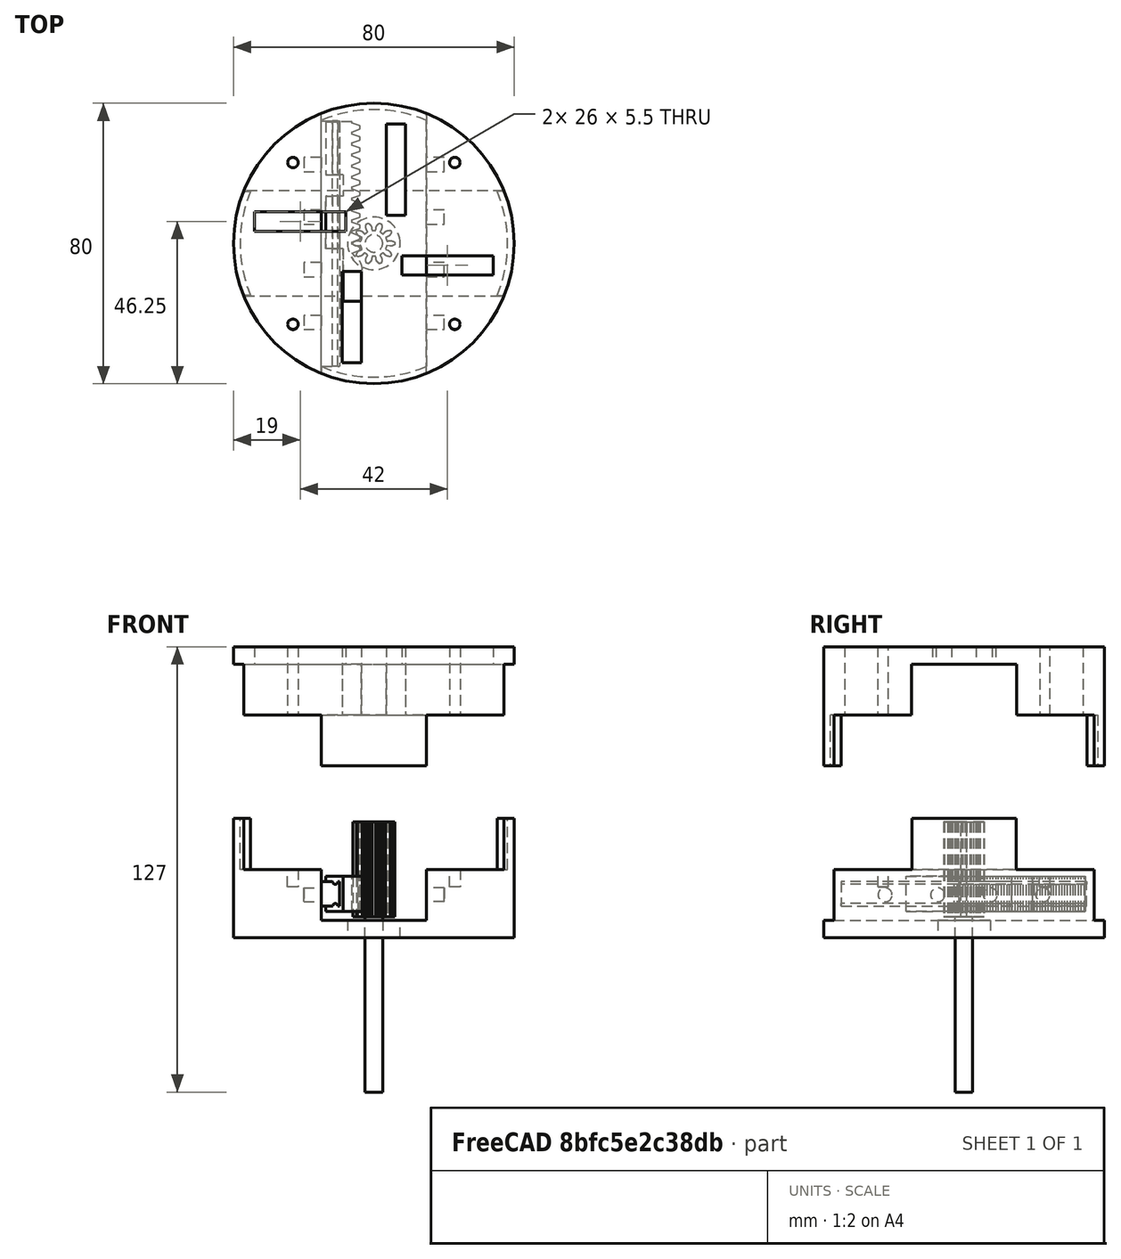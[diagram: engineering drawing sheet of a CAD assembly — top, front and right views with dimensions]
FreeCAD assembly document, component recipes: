
FREECAD ASSEMBLY — COMPONENT RECIPES ("2+2Jaw")

This assembly document has 7 components, labeled P0..P6 below (a component is one placed body or linked part). 7 of them carry a construction recipe — the FreeCAD feature program that regenerates the part from scratch, quoted from this document or its linked companion documents; the rest are supplied as boundary geometry only. No exploded tour is included for this assembly.
COMPONENT P0 — recipe-attached ("Jaw_Shell_Bottom001", modeled in this document).
Construction recipe (the document's own serialized feature program — sketch geometry with constraints, then the solid features built on it; lengths are millimeters unless a unit is written):

FEATURE [Sketcher::SketchObject] Sketch
  ArcFitTolerance = 1e-06
  AttachmentSupport = -> [Origin004]
  ExternalTypes = [0]
  FullyConstrained = true
  MakeInternals = false
  MapMode = 5
  _ExternalGeoVersion = 1
  sketch-geometry (2):
    g0: Circle CenterX=0 CenterY=0 CenterZ=0 NormalX=0 NormalY=0 NormalZ=1 AngleXU=0 Radius=40
    g1: Circle CenterX=0 CenterY=0 CenterZ=0 NormalX=0 NormalY=0 NormalZ=1 AngleXU=0 Radius=7.5
  constraints (4):
    c: Diameter(g0) = 80
    c: Coincident(g0,g-1)
    c: Diameter(g1) = 15
    c: Coincident(g1,g0)
FEATURE [PartDesign::Pad] Pad
  Direction = (0,0,1)
  Length = 34
  Length2 = 10
  Profile = -> Sketch
  ReferenceAxis = -> Sketch [N_Axis]
  Refine = true
  SideType = 0
  Suppressed = false
  Type = 0
  Type2 = 0
FEATURE [Part::DatumPlane] DatumPlane
  AttachmentSupport = -> [Origin004]
  MapMode = 5
  Placement = pos=(0,0,0) rot=(1,0,0;1.5708rad)
FEATURE [Sketcher::SketchObject] Sketch001
  ArcFitTolerance = 1e-06
  AttachmentSupport = -> [DatumPlane]
  ExternalGeometry = -> [Pad]
  ExternalTypes = [0,0,0]
  FullyConstrained = true
  MakeInternals = false
  MapMode = 5
  Placement = pos=(0,0,0) rot=(1,0,0;1.5708rad)
  _ExternalGeoVersion = 1
  sketch-geometry (5):
    g0: LineSegment StartX=-15 StartY=34 StartZ=0 EndX=-15 EndY=5 EndZ=0
    g1: LineSegment StartX=-15 StartY=5 StartZ=0 EndX=15 EndY=5 EndZ=0
    g2: LineSegment StartX=15 StartY=5 StartZ=0 EndX=15 EndY=34 EndZ=0
    g3: LineSegment StartX=-15 StartY=34 StartZ=0 EndX=0 EndY=34 EndZ=0
    g4: LineSegment StartX=0 StartY=34 StartZ=0 EndX=15 EndY=34 EndZ=0
  constraints (15):
    c: Coincident(g0,g1)
    c: Coincident(g1,g2)
    c: Vertical(g0)
    c: Vertical(g2)
    c: Horizontal(g1)
    c: Distance(g1,g-4) = 5
    c: Coincident(g0,g3)
    c: Horizontal(g3)
    c: Coincident(g3,g4)
    c: Horizontal(g4)
    c: PointOnObject(g3,g-2)
    c: Coincident(g4,g2)
    c: Equal(g3,g4)
    c: PointOnObject(g0,g-3)
    c: DistanceX(g1,g1) = 30
FEATURE [PartDesign::Pocket] Pocket
  BaseFeature = -> Pad
  Direction = (0,1,-2e-16)
  Length = 5
  Length2 = 5
  Profile = -> Sketch001
  ReferenceAxis = -> Sketch001 [N_Axis]
  Refine = true
  SideType = 2
  Suppressed = false
  Type = 1
  Type2 = 0
FEATURE [Sketcher::SketchObject] Sketch002
  ArcFitTolerance = 1e-06
  AttachmentSupport = -> [Pocket]
  ExternalGeometry = -> [Pocket]
  ExternalTypes = [0,0,0]
  FullyConstrained = true
  MakeInternals = false
  MapMode = 5
  Placement = pos=(0,0,34) rot=(0,0,1;0rad)
  _ExternalGeoVersion = 1
  sketch-geometry (16):
    g0: LineSegment StartX=35.1413 StartY=-14.85 StartZ=0 EndX=37.1413 EndY=-14.85 EndZ=0
    g1: LineSegment StartX=37.1413 StartY=14.85 StartZ=0 EndX=35.1413 EndY=14.85 EndZ=0
    g2: LineSegment [constr] StartX=37.1413 StartY=-14.85 StartZ=0 EndX=37.1413 EndY=0 EndZ=0
    g3: LineSegment [constr] StartX=37.1413 StartY=0 StartZ=0 EndX=37.1413 EndY=14.85 EndZ=0
    g4: ArcOfCircle CenterX=0 CenterY=0 CenterZ=0 NormalX=0 NormalY=0 NormalZ=1 AngleXU=0 Radius=38.1502 StartAngle=5.88337 EndAngle=6.683
    g5: LineSegment StartX=-35.1413 StartY=-14.85 StartZ=0 EndX=-37.1413 EndY=-14.85 EndZ=0
    g6: LineSegment StartX=-37.1413 StartY=14.85 StartZ=0 EndX=-35.1413 EndY=14.85 EndZ=0
    g7: LineSegment [constr] StartX=-37.1413 StartY=-14.85 StartZ=0 EndX=-37.1413 EndY=0 EndZ=0
    g8: LineSegment [constr] StartX=-37.1413 StartY=0 StartZ=0 EndX=-37.1413 EndY=14.85 EndZ=0
    g9: ArcOfCircle CenterX=0 CenterY=0 CenterZ=0 NormalX=0 NormalY=0 NormalZ=1 AngleXU=0 Radius=38.1502 StartAngle=2.74177 EndAngle=3.54141
    g10: LineSegment StartX=-37.1413 StartY=14.85 StartZ=0 EndX=-37.1413 EndY=40 EndZ=0
    g11: LineSegment StartX=-37.1413 StartY=40 StartZ=0 EndX=37.1413 EndY=40 EndZ=0
    g12: LineSegment StartX=-37.1413 StartY=-14.85 StartZ=0 EndX=-37.1413 EndY=-40 EndZ=0
    g13: LineSegment StartX=-37.1413 StartY=-40 StartZ=0 EndX=37.1413 EndY=-40 EndZ=0
    g14: LineSegment StartX=37.1413 StartY=-40 StartZ=0 EndX=37.1413 EndY=-14.85 EndZ=0
    g15: LineSegment StartX=37.1413 StartY=14.85 StartZ=0 EndX=37.1413 EndY=40 EndZ=0
  constraints (46):
    c: Horizontal(g0)
    c: Horizontal(g1)
    c: Coincident(g2,g0)
    c: PointOnObject(g2,g-1)
    c: Vertical(g2)
    c: Coincident(g3,g2)
    c: Coincident(g3,g1)
    c: Vertical(g3)
    c: Equal(g2,g3)
    c: PointOnObject(g1,g-3)
    c: Coincident(g4,g-3)
    c: Coincident(g4,g0)
    c: Coincident(g4,g1)
    c: Distance(g1,g1) = 2
    c: Horizontal(g5)
    c: Horizontal(g6)
    c: Coincident(g7,g5)
    c: Vertical(g7)
    c: Coincident(g8,g7)
    c: Coincident(g8,g6)
    c: Vertical(g8)
    c: Equal(g7,g8)
    c: Coincident(g9,g5)
    c: Coincident(g9,g6)
    c: Coincident(g9,g4)
    c: PointOnObject(g7,g-1)
    c: PointOnObject(g5,g-3)
    c: Equal(g7,g2)
    c: Distance(g5,g6) = 29.7
    c: Coincident(g6,g10)
    c: Vertical(g10)
    c: Coincident(g10,g11)
    c: Horizontal(g11)
    c: Coincident(g5,g12)
    c: Vertical(g12)
    c: Coincident(g12,g13)
    c: Horizontal(g13)
    c: Coincident(g13,g14)
    c: Coincident(g14,g0)
    c: Vertical(g14)
    c: Coincident(g15,g1)
    c: Coincident(g15,g11)
    c: Vertical(g15)
    c: Tangent(g13,g-3)
    c: Equal(g6,g1)
    c: Tangent(g11,g-3)
FEATURE [PartDesign::Pocket] Pocket001
  BaseFeature = -> Pocket
  Direction = (0,0,-1)
  Length = 14.5
  Length2 = 5
  Profile = -> Sketch002
  ReferenceAxis = -> Sketch002 [N_Axis]
  Refine = true
  SideType = 0
  Suppressed = false
  Type = 0
  Type2 = 0
FEATURE [Sketcher::SketchObject] Sketch003
  ArcFitTolerance = 1e-06
  AttachmentSupport = -> [Pocket001]
  ExternalGeometry = -> [Pocket001]
  ExternalTypes = [0,0,0,0]
  FullyConstrained = true
  MakeInternals = false
  MapMode = 5
  Placement = pos=(0,0,19.5) rot=(0,0,1;0rad)
  _ExternalGeoVersion = 1
  sketch-geometry (20):
    g0: Circle CenterX=-23.0923 CenterY=22.9991 CenterZ=0 NormalX=0 NormalY=0 NormalZ=1 AngleXU=0 Radius=1.5
    g1: ArcOfCircle [constr] CenterX=-45.3233 CenterY=45.1404 CenterZ=0 NormalX=0 NormalY=0 NormalZ=1 AngleXU=0 Radius=31.376 StartAngle=4.97621 EndAngle=6.02341
    g2: LineSegment [constr] StartX=-37.1413 StartY=14.85 StartZ=0 EndX=-23.0923 EndY=22.9991 EndZ=0
    g3: LineSegment [constr] StartX=-23.0923 StartY=22.9991 StartZ=0 EndX=-15 EndY=37.081 EndZ=0
    g4: LineSegment [constr] StartX=-37.1413 StartY=14.85 StartZ=0 EndX=-15 EndY=37.081 EndZ=0
    g5: ArcOfCircle [constr] CenterX=45.3233 CenterY=45.1404 CenterZ=0 NormalX=0 NormalY=0 NormalZ=1 AngleXU=0 Radius=31.376 StartAngle=3.40137 EndAngle=4.44857
    g6: ArcOfCircle [constr] CenterX=-45.3233 CenterY=-45.1404 CenterZ=0 NormalX=0 NormalY=0 NormalZ=1 AngleXU=0 Radius=31.376 StartAngle=0.259778 EndAngle=1.30698
    g7: ArcOfCircle [constr] CenterX=45.3233 CenterY=-45.1404 CenterZ=0 NormalX=0 NormalY=0 NormalZ=1 AngleXU=0 Radius=31.376 StartAngle=1.83462 EndAngle=2.88181
    g8: LineSegment [constr] StartX=-37.1413 StartY=-14.85 StartZ=0 EndX=-23.0923 EndY=-22.9991 EndZ=0
    g9: LineSegment [constr] StartX=-23.0923 StartY=-22.9991 StartZ=0 EndX=-15 EndY=-37.081 EndZ=0
    g10: LineSegment [constr] StartX=-15 StartY=-37.081 StartZ=0 EndX=-37.1413 EndY=-14.85 EndZ=0
    g11: LineSegment [constr] StartX=15 StartY=-37.081 StartZ=0 EndX=37.1413 EndY=-14.85 EndZ=0
    g12: LineSegment [constr] StartX=37.1413 StartY=-14.85 StartZ=0 EndX=23.0923 EndY=-22.9991 EndZ=0
    g13: LineSegment [constr] StartX=23.0923 StartY=-22.9991 StartZ=0 EndX=15 EndY=-37.081 EndZ=0
    g14: LineSegment [constr] StartX=15 StartY=37.081 StartZ=0 EndX=23.0923 EndY=22.9991 EndZ=0
    g15: LineSegment [constr] StartX=23.0923 StartY=22.9991 StartZ=0 EndX=37.1413 EndY=14.85 EndZ=0
    g16: LineSegment [constr] StartX=37.1413 StartY=14.85 StartZ=0 EndX=15 EndY=37.081 EndZ=0
    g17: Circle CenterX=23.0923 CenterY=22.9991 CenterZ=0 NormalX=0 NormalY=0 NormalZ=1 AngleXU=0 Radius=1.5
    g18: Circle CenterX=23.0923 CenterY=-22.9991 CenterZ=0 NormalX=0 NormalY=0 NormalZ=1 AngleXU=0 Radius=1.5
    g19: Circle CenterX=-23.0923 CenterY=-22.9991 CenterZ=0 NormalX=0 NormalY=0 NormalZ=1 AngleXU=0 Radius=1.5
  constraints (48):
    c: Diameter(g0) = 3
    c: Coincident(g1,g-6)
    c: Coincident(g1,g-6)
    c: PointOnObject(g0,g1)
    c: Coincident(g1,g2)
    c: Coincident(g2,g3)
    c: Coincident(g3,g1)
    c: Equal(g3,g2)
    c: Coincident(g2,g0)
    c: Coincident(g4,g1)
    c: Coincident(g4,g1)
    c: Angle(g2,g4) = 0.261799
    c: Coincident(g5,g-3)
    c: Coincident(g5,g-3)
    c: Coincident(g6,g-5)
    c: Coincident(g6,g-5)
    c: Coincident(g7,g-4)
    c: Coincident(g7,g-4)
    c: Coincident(g6,g8)
    c: Coincident(g8,g9)
    c: Coincident(g9,g6)
    c: Coincident(g9,g10)
    c: Coincident(g10,g8)
    c: Coincident(g7,g11)
    c: Coincident(g11,g12)
    c: Coincident(g12,g13)
    c: Coincident(g13,g11)
    c: Coincident(g5,g14)
    c: Coincident(g14,g15)
    c: Coincident(g15,g5)
    c: Coincident(g15,g16)
    c: Coincident(g16,g14)
    c: Equal(g8,g9)
    c: Equal(g15,g14)
    c: Equal(g12,g13)
    c: PointOnObject(g8,g6)
    c: PointOnObject(g12,g7)
    c: Coincident(g11,g7)
    c: PointOnObject(g14,g5)
    c: Angle(g10,g8) = 0.261799
    c: Angle(g12,g11) = 0.261799
    c: Angle(g16,g15) = 0.261799
    c: Coincident(g17,g14)
    c: Coincident(g18,g12)
    c: Coincident(g19,g8)
    c: Equal(g0,g17)
    c: Equal(g0,g19)
    c: Equal(g0,g18)
FEATURE [PartDesign::Pocket] Pocket002
  BaseFeature = -> Pocket001
  Direction = (0,0,-1)
  Length = 5
  Length2 = 5
  Profile = -> Sketch003
  ReferenceAxis = -> Sketch003 [N_Axis]
  Refine = true
  SideType = 0
  Suppressed = false
  Type = 0
  Type2 = 0
FEATURE [Sketcher::SketchObject] Sketch015
  ArcFitTolerance = 1e-06
  AttachmentSupport = -> [Pocket002]
  ExternalGeometry = -> [Pocket002]
  ExternalTypes = [0,0]
  FullyConstrained = true
  MakeInternals = false
  MapMode = 5
  Placement = pos=(-15,0,0) rot=(0.57735,0.57735,0.57735;2.0944rad)
  _ExternalGeoVersion = 1
  sketch-geometry (9):
    g0: Circle CenterX=22.5 CenterY=12.25 CenterZ=0 NormalX=0 NormalY=0 NormalZ=1 AngleXU=0 Radius=2
    g1: Circle CenterX=-22.5 CenterY=12.25 CenterZ=0 NormalX=0 NormalY=0 NormalZ=1 AngleXU=0 Radius=2
    g2: Circle CenterX=-7.5 CenterY=12.25 CenterZ=0 NormalX=0 NormalY=0 NormalZ=1 AngleXU=0 Radius=2
    g3: Circle CenterX=7.5 CenterY=12.25 CenterZ=0 NormalX=0 NormalY=0 NormalZ=1 AngleXU=0 Radius=2
    g4: LineSegment [constr] StartX=22.5 StartY=12.25 StartZ=0 EndX=7.5 EndY=12.25 EndZ=0
    g5: LineSegment [constr] StartX=7.5 StartY=12.25 StartZ=0 EndX=-7.5 EndY=12.25 EndZ=0
    g6: LineSegment [constr] StartX=-7.5 StartY=12.25 StartZ=0 EndX=-22.5 EndY=12.25 EndZ=0
    g7: LineSegment [constr] StartX=-22.5 StartY=12.25 StartZ=0 EndX=-37.081 EndY=12.25 EndZ=0
    g8: LineSegment [constr] StartX=22.5 StartY=12.25 StartZ=0 EndX=37.081 EndY=12.25 EndZ=0
  constraints (23):
    c: Diameter(g1) = 4
    c: Coincident(g0,g4)
    c: Coincident(g4,g3)
    c: Coincident(g4,g5)
    c: Coincident(g5,g2)
    c: Coincident(g5,g6)
    c: Coincident(g6,g1)
    c: Coincident(g6,g7)
    c: Horizontal(g7)
    c: Horizontal(g5)
    c: Horizontal(g6)
    c: Horizontal(g4)
    c: Equal(g1,g2)
    c: Equal(g1,g3)
    c: Equal(g1,g0)
    c: Equal(g6,g5)
    c: Equal(g6,g4)
    c: Equal(g8,g7)
    c: Horizontal(g8)
    c: PointOnObject(g7,g-4)
    c: Symmetric(g-3,g-3,g8)
    c: Coincident(g0,g8)
    c: DistanceX(g5,g5) = 15
FEATURE [Sketcher::SketchObject] Sketch016
  ArcFitTolerance = 1e-06
  AttachmentSupport = -> [Pocket002]
  ExternalGeometry = -> [Pocket002]
  ExternalTypes = [0,0]
  FullyConstrained = true
  MakeInternals = false
  MapMode = 5
  Placement = pos=(15,0,0) rot=(0.57735,-0.57735,-0.57735;2.0944rad)
  _ExternalGeoVersion = 1
  sketch-geometry (9):
    g0: Circle CenterX=22.5 CenterY=12.25 CenterZ=0 NormalX=0 NormalY=0 NormalZ=1 AngleXU=0 Radius=2
    g1: Circle CenterX=-22.5 CenterY=12.25 CenterZ=0 NormalX=0 NormalY=0 NormalZ=1 AngleXU=0 Radius=2
    g2: Circle CenterX=-7.5 CenterY=12.25 CenterZ=0 NormalX=0 NormalY=0 NormalZ=1 AngleXU=0 Radius=2
    g3: Circle CenterX=7.5 CenterY=12.25 CenterZ=0 NormalX=0 NormalY=0 NormalZ=1 AngleXU=0 Radius=2
    g4: LineSegment [constr] StartX=22.5 StartY=12.25 StartZ=0 EndX=7.5 EndY=12.25 EndZ=0
    g5: LineSegment [constr] StartX=7.5 StartY=12.25 StartZ=0 EndX=-7.5 EndY=12.25 EndZ=0
    g6: LineSegment [constr] StartX=-7.5 StartY=12.25 StartZ=0 EndX=-22.5 EndY=12.25 EndZ=0
    g7: LineSegment [constr] StartX=-22.5 StartY=12.25 StartZ=0 EndX=-37.081 EndY=12.25 EndZ=0
    g8: LineSegment [constr] StartX=22.5 StartY=12.25 StartZ=0 EndX=37.081 EndY=12.25 EndZ=0
  constraints (22):
    c: Diameter(g1) = 4
    c: Coincident(g0,g4)
    c: Coincident(g4,g3)
    c: Coincident(g4,g5)
    c: Coincident(g5,g2)
    c: Coincident(g5,g6)
    c: Coincident(g6,g1)
    c: Coincident(g6,g7)
    c: Horizontal(g7)
    c: Horizontal(g5)
    c: Horizontal(g6)
    c: Horizontal(g4)
    c: Equal(g1,g2)
    c: Equal(g1,g3)
    c: Equal(g1,g0)
    c: Equal(g6,g5)
    c: Equal(g6,g4)
    c: Equal(g8,g7)
    c: Symmetric(g-4,g-4,g8)
    c: Symmetric(g-3,g-3,g7)
    c: Coincident(g8,g0)
    c: DistanceX(g5,g5) = 15
FEATURE [PartDesign::Pocket] Pocket010
  BaseFeature = -> Pocket002
  Direction = (-1,0,0)
  Length = 5
  Length2 = 5
  Profile = -> Sketch015
  ReferenceAxis = -> Sketch015 [N_Axis]
  Refine = true
  SideType = 0
  Suppressed = false
  Type = 0
  Type2 = 0
FEATURE [PartDesign::Pocket] Pocket011
  BaseFeature = -> Pocket010
  Direction = (1,0,0)
  Length = 5
  Length2 = 5
  Profile = -> Sketch016
  ReferenceAxis = -> Sketch016 [N_Axis]
  Refine = true
  SideType = 0
  Suppressed = false
  Type = 0
  Type2 = 0
FEATURE [PartDesign::Body] Body  label="Jaw_Shell_Bottom"
  AllowCompound = true
  Group = -> [Sketch,Pad,DatumPlane,Sketch001,Pocket,Sketch002,Pocket001,Sketch003,Pocket002,Sketch015,Sketch016,Pocket010,Pocket011]
  Origin = -> Origin004
  Tip = -> Pocket011
COMPONENT P1 — recipe-attached ("Jaw_Shell_Top001", modeled in this document).
Construction recipe (the document's own serialized feature program — sketch geometry with constraints, then the solid features built on it; lengths are millimeters unless a unit is written):

FEATURE [Part::DatumPlane] DatumPlane001
  AttachmentSupport = -> [Origin006]
  MapMode = 5
  Placement = pos=(0,0,0) rot=(1,0,0;1.5708rad)
FEATURE [Sketcher::SketchObject] Sketch004
  ArcFitTolerance = 1e-06
  AttachmentSupport = -> [Origin006]
  ExternalTypes = [0]
  FullyConstrained = true
  MakeInternals = false
  MapMode = 5
  _ExternalGeoVersion = 1
  sketch-geometry (1):
    g0: Circle CenterX=0 CenterY=0 CenterZ=0 NormalX=0 NormalY=0 NormalZ=1 AngleXU=0 Radius=40
  constraints (2):
    c: Diameter(g0) = 80
    c: Coincident(g0,g-1)
FEATURE [PartDesign::Pad] Pad001
  Direction = (0,0,1)
  Length = 34
  Length2 = 10
  Profile = -> Sketch004
  ReferenceAxis = -> Sketch004 [N_Axis]
  Refine = true
  SideType = 0
  Suppressed = false
  Type = 0
  Type2 = 0
FEATURE [Sketcher::SketchObject] Sketch005
  ArcFitTolerance = 1e-06
  AttachmentSupport = -> [DatumPlane001]
  ExternalGeometry = -> [Pad001]
  ExternalTypes = [0,0,0]
  FullyConstrained = true
  MakeInternals = false
  MapMode = 5
  Placement = pos=(0,0,0) rot=(1,0,0;1.5708rad)
  _ExternalGeoVersion = 1
  sketch-geometry (5):
    g0: LineSegment StartX=-15 StartY=34 StartZ=0 EndX=-15 EndY=5 EndZ=0
    g1: LineSegment StartX=-15 StartY=5 StartZ=0 EndX=15 EndY=5 EndZ=0
    g2: LineSegment StartX=15 StartY=5 StartZ=0 EndX=15 EndY=34 EndZ=0
    g3: LineSegment StartX=-15 StartY=34 StartZ=0 EndX=0 EndY=34 EndZ=0
    g4: LineSegment StartX=0 StartY=34 StartZ=0 EndX=15 EndY=34 EndZ=0
  constraints (15):
    c: Coincident(g0,g1)
    c: Coincident(g1,g2)
    c: Vertical(g0)
    c: Vertical(g2)
    c: Horizontal(g1)
    c: Distance(g1,g-4) = 5
    c: Coincident(g0,g3)
    c: Horizontal(g3)
    c: Coincident(g3,g4)
    c: Horizontal(g4)
    c: PointOnObject(g3,g-2)
    c: Coincident(g4,g2)
    c: Equal(g3,g4)
    c: PointOnObject(g0,g-3)
    c: DistanceX(g1,g1) = 30
FEATURE [PartDesign::Pocket] Pocket003
  BaseFeature = -> Pad001
  Direction = (0,1,-2e-16)
  Length = 5
  Length2 = 5
  Profile = -> Sketch005
  ReferenceAxis = -> Sketch005 [N_Axis]
  Refine = true
  SideType = 2
  Suppressed = false
  Type = 1
  Type2 = 0
FEATURE [Sketcher::SketchObject] Sketch006
  ArcFitTolerance = 1e-06
  AttachmentSupport = -> [Pocket003]
  ExternalGeometry = -> [Pocket003]
  ExternalTypes = [0,0,0]
  FullyConstrained = true
  MakeInternals = false
  MapMode = 5
  Placement = pos=(0,0,34) rot=(0,0,1;0rad)
  _ExternalGeoVersion = 1
  sketch-geometry (16):
    g0: LineSegment StartX=35.081 StartY=-15 StartZ=0 EndX=37.081 EndY=-15 EndZ=0
    g1: LineSegment StartX=37.081 StartY=15 StartZ=0 EndX=35.081 EndY=15 EndZ=0
    g2: LineSegment [constr] StartX=37.081 StartY=-15 StartZ=0 EndX=37.081 EndY=0 EndZ=0
    g3: LineSegment [constr] StartX=37.081 StartY=0 StartZ=0 EndX=37.081 EndY=15 EndZ=0
    g4: ArcOfCircle CenterX=0 CenterY=0 CenterZ=0 NormalX=0 NormalY=0 NormalZ=1 AngleXU=0 Radius=38.1533 StartAngle=5.87913 EndAngle=6.68724
    g5: LineSegment StartX=-35.081 StartY=-15 StartZ=0 EndX=-37.081 EndY=-15 EndZ=0
    g6: LineSegment StartX=-37.081 StartY=15 StartZ=0 EndX=-35.081 EndY=15 EndZ=0
    g7: LineSegment [constr] StartX=-37.081 StartY=-15 StartZ=0 EndX=-37.081 EndY=0 EndZ=0
    g8: LineSegment [constr] StartX=-37.081 StartY=0 StartZ=0 EndX=-37.081 EndY=15 EndZ=0
    g9: ArcOfCircle CenterX=0 CenterY=0 CenterZ=0 NormalX=0 NormalY=0 NormalZ=1 AngleXU=0 Radius=38.1533 StartAngle=2.73754 EndAngle=3.54565
    g10: LineSegment StartX=-37.081 StartY=15 StartZ=0 EndX=-37.081 EndY=40 EndZ=0
    g11: LineSegment StartX=-37.081 StartY=40 StartZ=0 EndX=37.081 EndY=40 EndZ=0
    g12: LineSegment StartX=-37.081 StartY=-15 StartZ=0 EndX=-37.081 EndY=-40 EndZ=0
    g13: LineSegment StartX=-37.081 StartY=-40 StartZ=0 EndX=37.081 EndY=-40 EndZ=0
    g14: LineSegment StartX=37.081 StartY=-40 StartZ=0 EndX=37.081 EndY=-15 EndZ=0
    g15: LineSegment StartX=37.081 StartY=15 StartZ=0 EndX=37.081 EndY=40 EndZ=0
  constraints (46):
    c: Horizontal(g0)
    c: Horizontal(g1)
    c: Coincident(g2,g0)
    c: PointOnObject(g2,g-1)
    c: Vertical(g2)
    c: Coincident(g3,g2)
    c: Coincident(g3,g1)
    c: Vertical(g3)
    c: Equal(g2,g3)
    c: PointOnObject(g1,g-3)
    c: Coincident(g4,g-3)
    c: Coincident(g4,g0)
    c: Coincident(g4,g1)
    c: Distance(g1,g1) = 2
    c: Horizontal(g5)
    c: Horizontal(g6)
    c: Coincident(g7,g5)
    c: Vertical(g7)
    c: Coincident(g8,g7)
    c: Coincident(g8,g6)
    c: Vertical(g8)
    c: Equal(g7,g8)
    c: Coincident(g9,g5)
    c: Coincident(g9,g6)
    c: Coincident(g9,g4)
    c: PointOnObject(g7,g-1)
    c: PointOnObject(g5,g-3)
    c: Equal(g7,g2)
    c: Distance(g5,g6) = 30
    c: Coincident(g6,g10)
    c: Vertical(g10)
    c: Coincident(g10,g11)
    c: Horizontal(g11)
    c: Coincident(g5,g12)
    c: Vertical(g12)
    c: Coincident(g12,g13)
    c: Horizontal(g13)
    c: Coincident(g13,g14)
    c: Coincident(g14,g0)
    c: Vertical(g14)
    c: Coincident(g15,g1)
    c: Coincident(g15,g11)
    c: Vertical(g15)
    c: Tangent(g13,g-3)
    c: Equal(g6,g1)
    c: Tangent(g11,g-3)
FEATURE [PartDesign::Pocket] Pocket004
  BaseFeature = -> Pocket003
  Direction = (0,0,-1)
  Length = 14.5
  Length2 = 5
  Profile = -> Sketch006
  ReferenceAxis = -> Sketch006 [N_Axis]
  Refine = true
  SideType = 0
  Suppressed = false
  Type = 0
  Type2 = 0
FEATURE [Sketcher::SketchObject] Sketch007
  ArcFitTolerance = 1e-06
  AttachmentSupport = -> [Pocket004]
  ExternalGeometry = -> [Pocket004]
  ExternalTypes = [0,0,0,0]
  FullyConstrained = true
  MakeInternals = false
  MapMode = 5
  Placement = pos=(0,0,19.5) rot=(0,0,1;0rad)
  _ExternalGeoVersion = 1
  sketch-geometry (20):
    g0: Circle CenterX=-23.0822 CenterY=23.0822 CenterZ=0 NormalX=0 NormalY=0 NormalZ=1 AngleXU=0 Radius=1.5
    g1: ArcOfCircle [constr] CenterX=-45.1632 CenterY=45.1632 CenterZ=0 NormalX=0 NormalY=0 NormalZ=1 AngleXU=0 Radius=31.2272 StartAngle=4.97419 EndAngle=6.02139
    g2: LineSegment [constr] StartX=-37.081 StartY=15 StartZ=0 EndX=-23.0822 EndY=23.0822 EndZ=0
    g3: LineSegment [constr] StartX=-23.0822 StartY=23.0822 StartZ=0 EndX=-15 EndY=37.081 EndZ=0
    g4: LineSegment [constr] StartX=-37.081 StartY=15 StartZ=0 EndX=-15 EndY=37.081 EndZ=0
    g5: ArcOfCircle [constr] CenterX=45.1632 CenterY=45.1632 CenterZ=0 NormalX=0 NormalY=0 NormalZ=1 AngleXU=0 Radius=31.2272 StartAngle=3.40339 EndAngle=4.45059
    g6: ArcOfCircle [constr] CenterX=-45.1632 CenterY=-45.1632 CenterZ=0 NormalX=0 NormalY=0 NormalZ=1 AngleXU=0 Radius=31.2272 StartAngle=0.261799 EndAngle=1.309
    g7: ArcOfCircle [constr] CenterX=45.1632 CenterY=-45.1632 CenterZ=0 NormalX=0 NormalY=0 NormalZ=1 AngleXU=0 Radius=31.2272 StartAngle=1.8326 EndAngle=2.87979
    g8: LineSegment [constr] StartX=-37.081 StartY=-15 StartZ=0 EndX=-23.0822 EndY=-23.0822 EndZ=0
    g9: LineSegment [constr] StartX=-23.0822 StartY=-23.0822 StartZ=0 EndX=-15 EndY=-37.081 EndZ=0
    g10: LineSegment [constr] StartX=-15 StartY=-37.081 StartZ=0 EndX=-37.081 EndY=-15 EndZ=0
    g11: LineSegment [constr] StartX=15 StartY=-37.081 StartZ=0 EndX=37.081 EndY=-15 EndZ=0
    g12: LineSegment [constr] StartX=37.081 StartY=-15 StartZ=0 EndX=23.0822 EndY=-23.0822 EndZ=0
    g13: LineSegment [constr] StartX=23.0822 StartY=-23.0822 StartZ=0 EndX=15 EndY=-37.081 EndZ=0
    g14: LineSegment [constr] StartX=15 StartY=37.081 StartZ=0 EndX=23.0822 EndY=23.0822 EndZ=0
    g15: LineSegment [constr] StartX=23.0822 StartY=23.0822 StartZ=0 EndX=37.081 EndY=15 EndZ=0
    g16: LineSegment [constr] StartX=37.081 StartY=15 StartZ=0 EndX=15 EndY=37.081 EndZ=0
    g17: Circle CenterX=23.0822 CenterY=23.0822 CenterZ=0 NormalX=0 NormalY=0 NormalZ=1 AngleXU=0 Radius=1.5
    g18: Circle CenterX=23.0822 CenterY=-23.0822 CenterZ=0 NormalX=0 NormalY=0 NormalZ=1 AngleXU=0 Radius=1.5
    g19: Circle CenterX=-23.0822 CenterY=-23.0822 CenterZ=0 NormalX=0 NormalY=0 NormalZ=1 AngleXU=0 Radius=1.5
  constraints (48):
    c: Diameter(g0) = 3
    c: Coincident(g1,g-6)
    c: Coincident(g1,g-6)
    c: PointOnObject(g0,g1)
    c: Coincident(g1,g2)
    c: Coincident(g2,g3)
    c: Coincident(g3,g1)
    c: Equal(g3,g2)
    c: Coincident(g2,g0)
    c: Coincident(g4,g1)
    c: Coincident(g4,g1)
    c: Angle(g2,g4) = 0.261799
    c: Coincident(g5,g-3)
    c: Coincident(g5,g-3)
    c: Coincident(g6,g-5)
    c: Coincident(g6,g-5)
    c: Coincident(g7,g-4)
    c: Coincident(g7,g-4)
    c: Coincident(g6,g8)
    c: Coincident(g8,g9)
    c: Coincident(g9,g6)
    c: Coincident(g9,g10)
    c: Coincident(g10,g8)
    c: Coincident(g7,g11)
    c: Coincident(g11,g12)
    c: Coincident(g12,g13)
    c: Coincident(g13,g11)
    c: Coincident(g5,g14)
    c: Coincident(g14,g15)
    c: Coincident(g15,g5)
    c: Coincident(g15,g16)
    c: Coincident(g16,g14)
    c: Equal(g8,g9)
    c: Equal(g15,g14)
    c: Equal(g12,g13)
    c: PointOnObject(g8,g6)
    c: PointOnObject(g12,g7)
    c: Coincident(g11,g7)
    c: PointOnObject(g14,g5)
    c: Angle(g10,g8) = 0.261799
    c: Angle(g12,g11) = 0.261799
    c: Angle(g16,g15) = 0.261799
    c: Coincident(g17,g14)
    c: Coincident(g18,g12)
    c: Coincident(g19,g8)
    c: Equal(g0,g17)
    c: Equal(g0,g19)
    c: Equal(g0,g18)
FEATURE [PartDesign::Pocket] Pocket005
  BaseFeature = -> Pocket004
  Direction = (0,0,-1)
  Length = 5
  Length2 = 5
  Profile = -> Sketch007
  ReferenceAxis = -> Sketch007 [N_Axis]
  Refine = true
  SideType = 0
  Suppressed = false
  Type = 1
  Type2 = 0
FEATURE [Sketcher::SketchObject] Sketch014
  ArcFitTolerance = 1e-06
  AttachmentSupport = -> [Pocket004]
  ExternalTypes = [0]
  FullyConstrained = true
  MakeInternals = false
  MapMode = 5
  Placement = pos=(0,0,0) rot=(1,0,0;3.14159rad)
  _ExternalGeoVersion = 1
  sketch-geometry (24):
    g0: LineSegment StartX=3.5 StartY=34 StartZ=0 EndX=3.5 EndY=8 EndZ=0
    g1: LineSegment StartX=3.5 StartY=8 StartZ=0 EndX=9 EndY=8 EndZ=0
    g2: LineSegment StartX=9 StartY=8 StartZ=0 EndX=9 EndY=34 EndZ=0
    g3: LineSegment StartX=9 StartY=34 StartZ=0 EndX=3.5 EndY=34 EndZ=0
    g4: LineSegment StartX=8 StartY=-3.5 StartZ=0 EndX=8 EndY=-9 EndZ=0
    g5: LineSegment StartX=8 StartY=-9 StartZ=0 EndX=34 EndY=-9 EndZ=0
    g6: LineSegment StartX=34 StartY=-9 StartZ=0 EndX=34 EndY=-3.5 EndZ=0
    g7: LineSegment StartX=34 StartY=-3.5 StartZ=0 EndX=8 EndY=-3.5 EndZ=0
    g8: LineSegment StartX=-9 StartY=-8 StartZ=0 EndX=-9 EndY=-34 EndZ=0
    g9: LineSegment StartX=-9 StartY=-34 StartZ=0 EndX=-3.5 EndY=-34 EndZ=0
    g10: LineSegment StartX=-3.5 StartY=-34 StartZ=0 EndX=-3.5 EndY=-8 EndZ=0
    g11: LineSegment StartX=-3.5 StartY=-8 StartZ=0 EndX=-9 EndY=-8 EndZ=0
    g12: LineSegment StartX=-8 StartY=9 StartZ=0 EndX=-34 EndY=9 EndZ=0
    g13: LineSegment StartX=-34 StartY=9 StartZ=0 EndX=-34 EndY=3.5 EndZ=0
    g14: LineSegment StartX=-34 StartY=3.5 StartZ=0 EndX=-8 EndY=3.5 EndZ=0
    g15: LineSegment StartX=-8 StartY=3.5 StartZ=0 EndX=-8 EndY=9 EndZ=0
    g16: LineSegment [constr] StartX=3.5 StartY=0 StartZ=0 EndX=3.5 EndY=8 EndZ=0
    g17: LineSegment [constr] StartX=0 StartY=8 StartZ=0 EndX=3.5 EndY=8 EndZ=0
    g18: LineSegment [constr] StartX=-8 StartY=0 StartZ=0 EndX=-8 EndY=3.5 EndZ=0
    g19: LineSegment [constr] StartX=-8 StartY=3.5 StartZ=0 EndX=0 EndY=3.5 EndZ=0
    g20: LineSegment [constr] StartX=0 StartY=-8 StartZ=0 EndX=-3.5 EndY=-8 EndZ=0
    g21: LineSegment [constr] StartX=-3.5 StartY=-8 StartZ=0 EndX=-3.5 EndY=0 EndZ=0
    g22: LineSegment [constr] StartX=0 StartY=-3.5 StartZ=0 EndX=8 EndY=-3.5 EndZ=0
    g23: LineSegment [constr] StartX=8 StartY=0 StartZ=0 EndX=8 EndY=-3.5 EndZ=0
  constraints (72):
    c: Coincident(g0,g1)
    c: Coincident(g1,g2)
    c: Coincident(g2,g3)
    c: Coincident(g3,g0)
    c: Vertical(g0)
    c: Vertical(g2)
    c: Horizontal(g1)
    c: Horizontal(g3)
    c: Coincident(g4,g5)
    c: Coincident(g5,g6)
    c: Coincident(g6,g7)
    c: Coincident(g7,g4)
    c: Vertical(g4)
    c: Vertical(g6)
    c: Horizontal(g5)
    c: Horizontal(g7)
    c: Distance(g4,g6) = 26
    c: Distance(g5,g7) = 5.5
    c: Coincident(g8,g9)
    c: Coincident(g9,g10)
    c: Coincident(g10,g11)
    c: Coincident(g11,g8)
    c: Vertical(g8)
    c: Vertical(g10)
    c: Horizontal(g9)
    c: Horizontal(g11)
    c: Coincident(g12,g13)
    c: Coincident(g13,g14)
    c: Coincident(g14,g15)
    c: Coincident(g15,g12)
    c: Horizontal(g12)
    c: Horizontal(g14)
    c: Vertical(g13)
    c: Vertical(g15)
    c: Distance(g-1,g7) = 3.5
    c: Equal(g5,g2)
    c: Equal(g5,g14)
    c: Equal(g5,g8)
    c: PointOnObject(g16,g-1)
    c: Coincident(g16,g0)
    c: PointOnObject(g17,g-2)
    c: Coincident(g17,g0)
    c: PointOnObject(g18,g-1)
    c: Coincident(g18,g14)
    c: Coincident(g19,g14)
    c: PointOnObject(g19,g-2)
    c: Horizontal(g19)
    c: PointOnObject(g20,g-2)
    c: Coincident(g20,g10)
    c: Coincident(g21,g10)
    c: PointOnObject(g21,g-1)
    c: PointOnObject(g22,g-2)
    c: Coincident(g22,g4)
    c: PointOnObject(g23,g-1)
    c: Coincident(g23,g4)
    c: Horizontal(g17)
    c: Horizontal(g22)
    c: Horizontal(g20)
    c: Vertical(g21)
    c: Vertical(g18)
    c: Vertical(g23)
    c: Vertical(g16)
    c: Distance(g-2,g4) = 8
    c: Equal(g22,g16)
    c: Equal(g22,g19)
    c: Equal(g22,g21)
    c: Equal(g23,g17)
    c: Equal(g23,g18)
    c: Equal(g23,g20)
    c: Equal(g4,g1)
    c: Equal(g4,g11)
    c: Equal(g4,g15)
FEATURE [PartDesign::Pocket] Pocket009
  BaseFeature = -> Pocket005
  Direction = (0,0,1)
  Length = 5
  Length2 = 5
  Profile = -> Sketch014
  ReferenceAxis = -> Sketch014 [N_Axis]
  Refine = true
  SideType = 0
  Suppressed = false
  Type = 1
  Type2 = 0
FEATURE [PartDesign::Body] Body001  label="Jaw_Shell_Top"
  AllowCompound = true
  Group = -> [Sketch004,Pad001,DatumPlane001,Sketch005,Pocket003,Sketch006,Pocket004,Sketch007,Pocket005,Sketch014,Pocket009]
  Origin = -> Origin006
  Placement = pos=(-3.8e-15,3.8e-15,83) rot=(0.707107,0.707107,0;3.14159rad)
  Tip = -> Pocket009
COMPONENT P2 — recipe-attached ("Rack001", modeled in this document).
Construction recipe (the document's own serialized feature program — sketch geometry with constraints, then the solid features built on it; lengths are millimeters unless a unit is written):

FEATURE [PartDesign::FeaturePython] InvoluteRack  # WARN: FeaturePython — macro-defined, semantics opaque (R4)
  AttacherType = Attacher::AttachEngine3D
  Suppressed = false
  add_endings = true
  clearance = 0.25
  double_helix = false
  head = 0
  head_fillet = 0
  height = 10
  helix_angle = 0
  module = 1
  num_teeth = 12
  pressure_angle = 20
  properties_from_tool = false
  root_fillet = 0
  simplified = false
  thickness = 1
  transverse_pitch = 3.14159
  version = 1.3.0
FEATURE [Sketcher::SketchObject] Sketch009
  ArcFitTolerance = 1e-06
  AttachmentSupport = -> [InvoluteRack]
  ExternalGeometry = -> [InvoluteRack]
  ExternalTypes = [0,0,0]
  FullyConstrained = true
  MakeInternals = false
  MapMode = 5
  Placement = pos=(0,0,0) rot=(1,0,0;3.14159rad)
  _ExternalGeoVersion = 1
  sketch-geometry (10):
    g0: ArcOfCircle CenterX=2.74624 CenterY=-1.76464 CenterZ=0 NormalX=0 NormalY=0 NormalZ=1 AngleXU=0 Radius=5 StartAngle=2.2143 EndAngle=3.10281
    g1: LineSegment StartX=-3.75 StartY=-36.1283 StartZ=0 EndX=-3.75 EndY=15 EndZ=0
    g2: LineSegment StartX=-3.75 StartY=15 StartZ=0 EndX=1.74624 EndY=15 EndZ=0
    g3: LineSegment StartX=1.74624 StartY=15 StartZ=0 EndX=1.74624 EndY=6.23536 EndZ=0
    g4: ArcOfCircle CenterX=-3.25376 CenterY=6.23536 CenterZ=0 NormalX=0 NormalY=0 NormalZ=1 AngleXU=0 Radius=5 StartAngle=5.35589 EndAngle=6.28319
    g5: LineSegment [constr] StartX=2.74624 StartY=-1.76464 StartZ=0 EndX=2.74624 EndY=15 EndZ=0
    g6: LineSegment [constr] StartX=1.74624 StartY=15 StartZ=0 EndX=2.74624 EndY=15 EndZ=0
    g7: LineSegment [constr] StartX=-2.25 StartY=-1.5708 StartZ=0 EndX=-1.25 EndY=-1.5708 EndZ=0
    g8: LineSegment StartX=-2.25 StartY=-1.5708 StartZ=0 EndX=-2.25 EndY=-36.1283 EndZ=0
    g9: LineSegment StartX=-2.25 StartY=-36.1283 StartZ=0 EndX=-3.75 EndY=-36.1283 EndZ=0
  constraints (27):
    c: Radius(g0) = 5
    c: Vertical(g1)
    c: Coincident(g1,g2)
    c: Horizontal(g2)
    c: Coincident(g2,g3)
    c: Vertical(g3)
    c: Coincident(g5,g0)
    c: Vertical(g5)
    c: Coincident(g6,g2)
    c: Coincident(g6,g5)
    c: Horizontal(g6)
    c: Tangent(g4,g0) = 1.5708
    c: Tangent(g4,g3) = 1.5708
    c: PointOnObject(g-3,g0)
    c: Distance(g-1,g2) = 15
    c: Equal(g4,g0)
    c: Coincident(g7,g0)
    c: Symmetric(g-4,g-4,g7)
    c: Horizontal(g7)
    c: Distance(g3,g5) = 1
    c: Coincident(g8,g0)
    c: Coincident(g8,g-5)
    c: Vertical(g8)
    c: Coincident(g9,g8)
    c: Coincident(g9,g1)
    c: Horizontal(g9)
    c: Distance(g9,g9) = 1.5
FEATURE [PartDesign::Pad] Pad006
  BaseFeature = -> InvoluteRack
  Direction = (0,0,-1)
  Length = 10
  Length2 = 10
  Profile = -> Sketch009
  ReferenceAxis = -> Sketch009 [N_Axis]
  Refine = true
  SideType = 0
  Suppressed = false
  Type = 3
  Type2 = 0
  UpToFace = -> InvoluteRack [Face54]
FEATURE [Sketcher::SketchObject] Sketch010
  ArcFitTolerance = 1e-06
  AttachmentSupport = -> [Pad006]
  ExternalGeometry = -> [Pad006]
  ExternalTypes = [0]
  FullyConstrained = true
  MakeInternals = false
  MapMode = 5
  Placement = pos=(-3.75,0,0) rot=(0.57735,-0.57735,-0.57735;2.0944rad)
  _ExternalGeoVersion = 1
  sketch-geometry (8):
    g0: LineSegment StartX=-36.1283 StartY=10 StartZ=0 EndX=-36.1283 EndY=0 EndZ=0
    g1: LineSegment StartX=-36.1283 StartY=0 StartZ=0 EndX=-21.1283 EndY=0 EndZ=0
    g2: LineSegment StartX=-21.1283 StartY=0 StartZ=0 EndX=-21.1283 EndY=10 EndZ=0
    g3: LineSegment StartX=-21.1283 StartY=10 StartZ=0 EndX=-36.1283 EndY=10 EndZ=0
    g4: LineSegment StartX=0 StartY=0 StartZ=0 EndX=0 EndY=10 EndZ=0
    g5: LineSegment StartX=0 StartY=10 StartZ=0 EndX=-15 EndY=10 EndZ=0
    g6: LineSegment StartX=-15 StartY=10 StartZ=0 EndX=-15 EndY=0 EndZ=0
    g7: LineSegment StartX=-15 StartY=0 StartZ=0 EndX=0 EndY=0 EndZ=0
  constraints (22):
    c: Coincident(g0,g1)
    c: Coincident(g1,g2)
    c: Coincident(g2,g3)
    c: Coincident(g3,g0)
    c: Vertical(g0)
    c: Vertical(g2)
    c: Horizontal(g1)
    c: Horizontal(g3)
    c: Distance(g0,g2) = 15
    c: PointOnObject(g1,g-1)
    c: Coincident(g4,g5)
    c: Coincident(g5,g6)
    c: Coincident(g6,g7)
    c: Coincident(g7,g4)
    c: Vertical(g4)
    c: Vertical(g6)
    c: Horizontal(g5)
    c: Horizontal(g7)
    c: Distance(g4,g6) = 15
    c: Coincident(g4,g-1)
    c: Coincident(g0,g-3)
    c: PointOnObject(g5,g-3)
FEATURE [PartDesign::Pad] Pad007
  BaseFeature = -> Pad006
  Direction = (-1,0,0)
  Length = 5
  Length2 = 10
  Profile = -> Sketch010
  ReferenceAxis = -> Sketch010 [N_Axis]
  Refine = true
  SideType = 0
  Suppressed = false
  Type = 0
  Type2 = 0
FEATURE [Sketcher::SketchObject] Sketch011
  ArcFitTolerance = 1e-06
  AttachmentSupport = -> [Pad007]
  ExternalTypes = [0,0]
  FullyConstrained = true
  MakeInternals = false
  MapMode = 5
  Placement = pos=(-3.22e-14,36.1283,0) rot=(0,0.707107,0.707107;3.14159rad)
  _ExternalGeoVersion = 1
  sketch-geometry (14):
    g0: LineSegment StartX=8.75 StartY=1.5 StartZ=0 EndX=6.75 EndY=1.5 EndZ=0
    g1: LineSegment StartX=5.25 StartY=1.5 StartZ=0 EndX=4.75 EndY=1.5 EndZ=0
    g2: LineSegment StartX=4.75 StartY=1.5 StartZ=0 EndX=4.75 EndY=8.5 EndZ=0
    g3: LineSegment StartX=4.75 StartY=8.5 StartZ=0 EndX=5.25 EndY=8.5 EndZ=0
    g4: LineSegment StartX=6.75 StartY=8.5 StartZ=0 EndX=8.75 EndY=8.5 EndZ=0
    g5: LineSegment StartX=8.75 StartY=8.5 StartZ=0 EndX=8.75 EndY=1.5 EndZ=0
    g6: ArcOfCircle CenterX=6 CenterY=1.5 CenterZ=0 NormalX=0 NormalY=0 NormalZ=1 AngleXU=0 Radius=0.75 StartAngle=-1.8e-15 EndAngle=3.14159
    g7: ArcOfCircle CenterX=6 CenterY=8.5 CenterZ=0 NormalX=0 NormalY=0 NormalZ=1 AngleXU=0 Radius=0.75 StartAngle=3.14159 EndAngle=6.28318
    g8: LineSegment [constr] StartX=5.25 StartY=1.5 StartZ=0 EndX=5.25 EndY=8.5 EndZ=0
    g9: LineSegment [constr] StartX=6.75 StartY=8.5 StartZ=0 EndX=6.75 EndY=1.5 EndZ=0
    g10: LineSegment [constr] StartX=8.75 StartY=8.5 StartZ=0 EndX=8.75 EndY=10 EndZ=0
    g11: LineSegment [constr] StartX=8.75 StartY=1.5 StartZ=0 EndX=8.75 EndY=0 EndZ=0
    g12: LineSegment [constr] StartX=5.25 StartY=1.5 StartZ=0 EndX=6.75 EndY=1.5 EndZ=0
    g13: LineSegment [constr] StartX=5.25 StartY=8.5 StartZ=0 EndX=6.75 EndY=8.5 EndZ=0
  constraints (38):
    c: PointOnObject(g0,g-3)
    c: Horizontal(g0)
    c: Horizontal(g1)
    c: Coincident(g2,g1)
    c: Vertical(g2)
    c: Coincident(g3,g2)
    c: Horizontal(g3)
    c: PointOnObject(g4,g-3)
    c: Horizontal(g4)
    c: Coincident(g5,g4)
    c: Coincident(g5,g0)
    c: Coincident(g6,g1)
    c: Coincident(g6,g0)
    c: Coincident(g7,g3)
    c: Coincident(g7,g4)
    c: Equal(g7,g6)
    c: Coincident(g8,g1)
    c: Coincident(g8,g3)
    c: Vertical(g8)
    c: Coincident(g9,g4)
    c: Coincident(g9,g0)
    c: Vertical(g9)
    c: Coincident(g10,g4)
    c: Coincident(g10,g-3)
    c: Coincident(g11,g0)
    c: Coincident(g11,g-3)
    c: Equal(g11,g10)
    c: Coincident(g12,g1)
    c: Coincident(g12,g0)
    c: Coincident(g13,g3)
    c: Coincident(g13,g4)
    c: Horizontal(g13)
    c: Horizontal(g12)
    c: PointOnObject(g6,g12)
    c: Radius(g6) = 0.75
    c: Distance(g5,g2) = 4
    c: DistanceY(g2,g2) = 7
    c: DistanceX(g1,g1) = 0.5
FEATURE [PartDesign::Pocket] Pocket008
  BaseFeature = -> Pad007
  Direction = (0,-1,2e-16)
  Length = 5
  Length2 = 5
  Profile = -> Sketch011
  ReferenceAxis = -> Sketch011 [N_Axis]
  Refine = true
  SideType = 0
  Suppressed = false
  Type = 3
  Type2 = 0
  UpToFace = -> Pad007 [Face54]
FEATURE [PartDesign::Body] Body002  label="Rack"
  AllowCompound = false
  Group = -> [InvoluteRack,Sketch009,Pad006,Sketch010,Pad007,Sketch011,Pocket008]
  Origin = -> Origin008
  Placement = pos=(-5,-1.5,7.5) rot=(0,0,1;0rad)
  Tip = -> Pocket008
COMPONENT P3 — same part as P2; its construction recipe is shown at P2.
COMPONENT P4 — recipe-attached ("Rail001", modeled in this document).
Construction recipe (the document's own serialized feature program — sketch geometry with constraints, then the solid features built on it; lengths are millimeters unless a unit is written):

FEATURE [Sketcher::SketchObject] Sketch012
  ArcFitTolerance = 1e-06
  AttachmentSupport = -> [Origin012]
  ExternalTypes = [0]
  FullyConstrained = true
  MakeInternals = false
  MapMode = 5
  _ExternalGeoVersion = 1
  sketch-geometry (4):
    g0: LineSegment StartX=0 StartY=0 StartZ=0 EndX=70 EndY=0 EndZ=0
    g1: LineSegment StartX=70 StartY=0 StartZ=0 EndX=70 EndY=7 EndZ=0
    g2: LineSegment StartX=70 StartY=7 StartZ=0 EndX=0 EndY=7 EndZ=0
    g3: LineSegment StartX=0 StartY=7 StartZ=0 EndX=0 EndY=0 EndZ=0
  constraints (11):
    c: Coincident(g0,g1)
    c: Coincident(g1,g2)
    c: Coincident(g2,g3)
    c: Coincident(g3,g0)
    c: Horizontal(g0)
    c: Horizontal(g2)
    c: Vertical(g1)
    c: Vertical(g3)
    c: Distance(g1,g3) = 70
    c: Distance(g0,g2) = 7
    c: Coincident(g0,g-1)
FEATURE [PartDesign::Pad] Pad005
  Direction = (0,0,1)
  Length = 5.25
  Length2 = 10
  Profile = -> Sketch012
  ReferenceAxis = -> Sketch012 [N_Axis]
  Refine = true
  SideType = 0
  Suppressed = false
  Type = 0
  Type2 = 0
FEATURE [Sketcher::SketchObject] Sketch013
  ArcFitTolerance = 1e-06
  AttachmentSupport = -> [Pad005]
  ExternalGeometry = -> [Pad005]
  ExternalTypes = [0,0,0]
  FullyConstrained = true
  MakeInternals = false
  MapMode = 5
  Placement = pos=(0,0,0) rot=(0.57735,-0.57735,-0.57735;2.0944rad)
  _ExternalGeoVersion = 1
  sketch-geometry (5):
    g0: LineSegment StartX=-7 StartY=4.75 StartZ=0 EndX=-7 EndY=3.25 EndZ=0
    g1: ArcOfCircle CenterX=-7 CenterY=4 CenterZ=0 NormalX=0 NormalY=0 NormalZ=1 AngleXU=0 Radius=0.75 StartAngle=4.71239 EndAngle=7.85398
    g2: LineSegment StartX=-2.6e-15 StartY=4.75 StartZ=0 EndX=-2.6e-15 EndY=3.25 EndZ=0
    g3: ArcOfCircle CenterX=-1.20374e-05 CenterY=4 CenterZ=0 NormalX=0 NormalY=0 NormalZ=1 AngleXU=0 Radius=0.75 StartAngle=1.57078 EndAngle=4.71241
    g4: LineSegment [constr] StartX=-2.6e-15 StartY=4.75 StartZ=0 EndX=-7 EndY=4.75 EndZ=0
  constraints (16):
    c: PointOnObject(g0,g-4)
    c: PointOnObject(g2,g-5)
    c: Coincident(g4,g2)
    c: Coincident(g4,g0)
    c: Horizontal(g4)
    c: Tangent(g4,g3)
    c: Coincident(g1,g0)
    c: Radius(g1) = 0.75
    c: Distance(g-3,g4) = 0.5
    c: Coincident(g1,g0)
    c: Coincident(g2,g3)
    c: Equal(g1,g3)
    c: Vertical(g0)
    c: PointOnObject(g1,g0)
    c: Vertical(g2)
    c: Coincident(g3,g2)
FEATURE [PartDesign::Pocket] Pocket007
  BaseFeature = -> Pad005
  Direction = (1,0,0)
  Length = 5
  Length2 = 5
  Profile = -> Sketch013
  ReferenceAxis = -> Sketch013 [N_Axis]
  Refine = true
  SideType = 0
  Suppressed = false
  Type = 3
  Type2 = 0
  UpToFace = -> Pad005 [Face2]
FEATURE [PartDesign::Body] Body004  label="Rail"
  AllowCompound = false
  Group = -> [Sketch012,Pad005,Sketch013,Pocket007]
  Origin = -> Origin012
  Placement = pos=(-15,-35,9) rot=(0.57735,0.57735,0.57735;2.0944rad)
  Tip = -> Pocket007
COMPONENT P5 — same part as P4; its construction recipe is shown at P4.
COMPONENT P6 — recipe-attached ("Shaft001", modeled in this document).
Construction recipe (the document's own serialized feature program — sketch geometry with constraints, then the solid features built on it; lengths are millimeters unless a unit is written):

FEATURE [PartDesign::FeaturePython] InvoluteGear  # WARN: FeaturePython — macro-defined, semantics opaque (R4)
  AttacherType = Attacher::AttachEngine3D
  Suppressed = false
  addendum_diameter = 12
  angular_backlash = 0
  axle_hole = false
  axle_holesize = 10
  backlash = 0
  clearance = 0.25
  double_helix = false
  head = 0
  head_fillet = 0
  height = 27
  helix_angle = 0
  module = 1
  num_teeth = 10
  numpoints = 20
  offset_hole = false
  offset_holeoffset = 10
  offset_holesize = 10
  pitch_diameter = 10
  pressure_angle = 20
  properties_from_tool = false
  reversed_backlash = false
  root_diameter = 7.5
  root_fillet = 0
  shift = 0
  simple = false
  transverse_pitch = 3.14159
  traverse_module = 1
  undercut = false
  version = 1.3.0
  expr: angular_backlash = backlash / pitch_diameter * 360 ° / pi
FEATURE [Sketcher::SketchObject] Sketch008
  ArcFitTolerance = 1e-06
  AttachmentSupport = -> [InvoluteGear]
  ExternalTypes = [0]
  FullyConstrained = true
  MakeInternals = false
  MapMode = 5
  Placement = pos=(0,0,27) rot=(0,0,1;0rad)
  _ExternalGeoVersion = 1
  sketch-geometry (1):
    g0: Circle CenterX=0 CenterY=0 CenterZ=0 NormalX=0 NormalY=0 NormalZ=1 AngleXU=0 Radius=2.5
  constraints (2):
    c: Diameter(g0) = 5
    c: Coincident(g0,g-1)
FEATURE [PartDesign::Pad] Pad002
  BaseFeature = -> InvoluteGear
  Direction = (0,0,1)
  Length = 50
  Length2 = 10
  Profile = -> Sketch008
  ReferenceAxis = -> Sketch008 [N_Axis]
  Refine = true
  SideType = 0
  Suppressed = false
  Type = 0
  Type2 = 0
FEATURE [PartDesign::Body] Body003  label="Shaft"
  AllowCompound = false
  Group = -> [InvoluteGear,Sketch008,Pad002]
  Origin = -> Origin010
  Placement = pos=(0,4e-15,33) rot=(1,0,0;3.14159rad)
  Tip = -> Pad002
PROVENANCE & LICENSES
A FreeCAD (.FCStd) document from a public repository crawl; recipes are the document's own serialized feature recipes (and, for linked parts, companion documents' recipes).
License: as declared in the source repository (recorded in the dataset sidecar).
